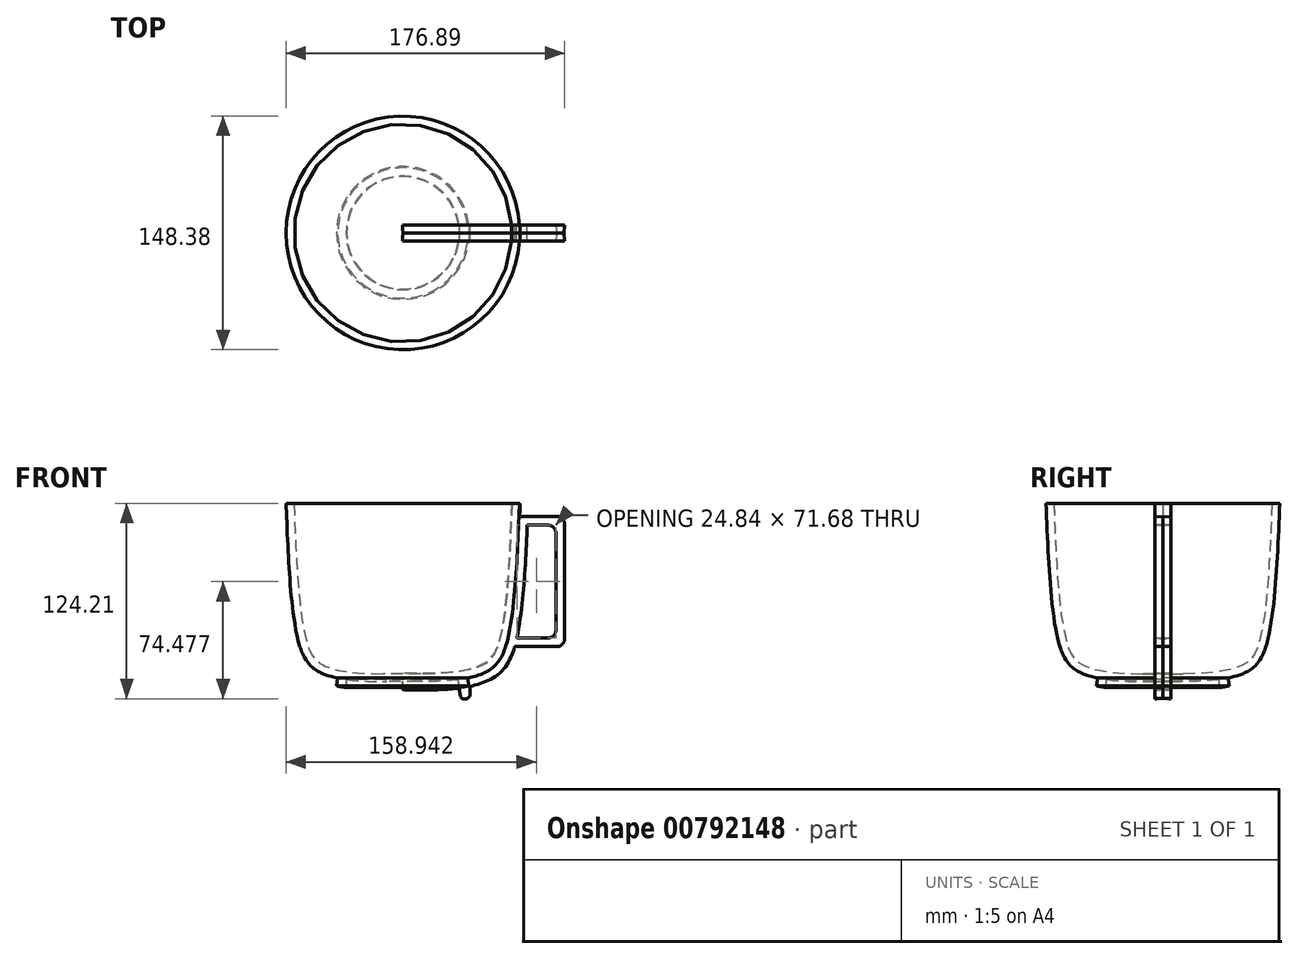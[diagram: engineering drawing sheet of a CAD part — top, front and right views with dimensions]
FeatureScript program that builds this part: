
annotation { "Feature Type Name" : "Feature", "Feature Type Description" : "" }
export const myFeature = defineFeature(function(context is Context, id is Id, definition is map)
    precondition{}
    {
        {
            var Q0;
            Q0=qCreatedBy(makeId("Front.planeOp"),FACE);
            var sketch = newSketch(context, id + "F0", { "sketchPlane" : qUnion([Q0])});
            skFitSpline(sketch, "E0", {"points": [v(74.37, 56.66) * mm, v(67.02, -32.92) * mm, v(51.64, -55.65) * mm, v(-23.23, -60) * mm], "startDerivative": vector(-9.7, -255.08) * mm, "endDerivative": vector(-242.27, 10.34) * mm});
            skFitSpline(sketch, "E1", {"points": [v(41.42, -58.78) * mm, v(41.61, -71.03) * mm, v(38.6, -71.7) * mm, v(37.27, -71.36) * mm, v(35.72, -59.72) * mm], "startDerivative": vector(7.18, -45.02) * mm, "endDerivative": vector(-2.54, 45.05) * mm});
            skFitSpline(sketch, "E2.0", {"points": [v(69.38, 56.85) * mm, v(69.17, 51.53) * mm, v(68.77, 40.91) * mm, v(68.1, 25.32) * mm, v(67.26, 10.36) * mm, v(66.22, -3.63) * mm, v(65.1, -14.23) * mm, v(64.03, -21.9) * mm, v(63.28, -26.32) * mm, v(62.63, -29.6) * mm, v(62.12, -31.94) * mm, v(61.6, -34.13) * mm, v(60.84, -36.84) * mm, v(59.83, -39.87) * mm, v(58.44, -42.92) * mm, v(56.86, -45.44) * mm, v(55.04, -47.54) * mm, v(53.22, -49.04) * mm, v(51.5, -50.13) * mm, v(50.05, -50.9) * mm, v(48.42, -51.62) * mm, v(46, -52.51) * mm, v(42.51, -53.5) * mm, v(37.7, -54.43) * mm, v(30.53, -55.37) * mm, v(20.35, -56) * mm, v(6.7, -56.06) * mm, v(-7.9, -55.65) * mm, v(-17.97, -55.22) * mm, v(-23.02, -55) * mm]});
            skLineSegment(sketch, "E3", {"start": v(69.2, 51.98) * mm, "end": v(74.2, 51.98) * mm});
            skLineSegment(sketch, "E4", {"start": v(0, 0) * mm, "end": v(0, -74.7) * mm});
            skLineSegment(sketch, "E5.bottom", {"start": v(97.44, 38.6) * mm, "end": v(78.67, 38.6) * mm});
            skLineSegment(sketch, "E5.top", {"start": v(97.44, -33.6) * mm, "end": v(72, -33.6) * mm});
            skLineSegment(sketch, "E5.left", {"start": v(97.44, 38.6) * mm, "end": v(97.44, -33.6) * mm});
            skLineSegment(sketch, "E6.0", {"start": v(102.44, 43.6) * mm, "end": v(73.87, 43.6) * mm});
            skLineSegment(sketch, "E6.1", {"start": v(102.44, 43.6) * mm, "end": v(102.44, -38.6) * mm});
            skLineSegment(sketch, "E6.2", {"start": v(102.44, -38.6) * mm, "end": v(65.5, -38.6) * mm});
            skFitSpline(sketch, "E7.0", {"points": [v(69.38, 56.85) * mm, v(69.17, 51.53) * mm, v(68.77, 40.91) * mm, v(68.1, 25.32) * mm, v(67.26, 10.36) * mm, v(66.22, -3.63) * mm, v(65.1, -14.23) * mm, v(64.03, -21.9) * mm, v(63.28, -26.32) * mm, v(62.63, -29.6) * mm, v(62.12, -31.94) * mm, v(61.6, -34.13) * mm, v(60.84, -36.84) * mm, v(59.83, -39.87) * mm, v(58.44, -42.92) * mm, v(56.86, -45.44) * mm, v(55.04, -47.54) * mm, v(53.22, -49.04) * mm, v(51.5, -50.13) * mm, v(50.05, -50.9) * mm, v(48.42, -51.62) * mm, v(46, -52.51) * mm, v(42.51, -53.5) * mm, v(37.7, -54.43) * mm, v(30.53, -55.37) * mm, v(20.35, -56) * mm, v(6.7, -56.06) * mm, v(-7.9, -55.65) * mm, v(-17.97, -55.22) * mm, v(-23.02, -55) * mm]});
            skFitSpline(sketch, "E8.trimOffspring", {"points": [v(79.37, 56.47) * mm, v(79.17, 51.15) * mm, v(78.76, 40.52) * mm, v(78.08, 24.83) * mm, v(77.24, 9.73) * mm, v(76.36, -2.13) * mm, v(75.5, -11.04) * mm, v(74.75, -17.4) * mm, v(73.92, -23.41) * mm, v(73.12, -28.1) * mm, v(72.43, -31.63) * mm, v(71.87, -34.18) * mm, v(71.28, -36.62) * mm, v(70.41, -39.76) * mm, v(69.17, -43.46) * mm, v(67.32, -47.58) * mm, v(64.98, -51.36) * mm, v(62.06, -54.73) * mm, v(58.54, -57.62) * mm, v(55.14, -59.59) * mm, v(52.15, -60.9) * mm, v(49, -62.07) * mm, v(44.77, -63.25) * mm, v(39.26, -64.31) * mm, v(31.38, -65.34) * mm, v(20.61, -66) * mm, v(6.55, -66.06) * mm, v(-8.28, -65.64) * mm, v(-18.4, -65.2) * mm, v(-23.44, -65) * mm]});
            skSolve(sketch);
        }
        {
            var Q0;
            {var subQ0=sQuery(id+"F0.wireOp",EDGE,"E3");var subQ1=sQuery(id+"F0.wireOp",EDGE,"E0");var subQ2=makeQuery(id+"F0.imprint","INTERSECT",VERTEX,{"derivedFrom":[subQ1,subQ0]});Q0=makeQuery(id+"F0.imprint","IMPRINT",FACE,{"disambiguationData":[TD([[makeQuery(id+"F0.imprint","IMPRINT",EDGE,{"disambiguationData":[TD([[subQ2,-1.0]])],"derivedFrom":subQ1}),-1.0]])]});}
            var Q1;
            {var subQ0=sQuery(id+"F0.wireOp",EDGE,"E6.0");var subQ1=sQuery(id+"F0.wireOp",EDGE,"E0");var subQ2=makeQuery(id+"F0.imprint","INTERSECT",VERTEX,{"derivedFrom":[subQ1,subQ0]});Q1=makeQuery(id+"F0.imprint","IMPRINT",FACE,{"disambiguationData":[TD([[makeQuery(id+"F0.imprint","IMPRINT",EDGE,{"disambiguationData":[TD([[subQ2,-1.0]])],"derivedFrom":subQ1}),-1.0]])]});}
            var Q2;
            {var subQ0=sQuery(id+"F0.wireOp",EDGE,"E5.bottom");var subQ1=sQuery(id+"F0.wireOp",EDGE,"E0");var subQ2=makeQuery(id+"F0.imprint","INTERSECT",VERTEX,{"derivedFrom":[subQ1,subQ0]});Q2=makeQuery(id+"F0.imprint","IMPRINT",FACE,{"disambiguationData":[TD([[makeQuery(id+"F0.imprint","IMPRINT",EDGE,{"disambiguationData":[TD([[subQ2,-1.0]])],"derivedFrom":subQ1}),-1.0]])]});}
            var Q3;
            {var subQ0=sQuery(id+"F0.wireOp",EDGE,"E1");var subQ1=sQuery(id+"F0.wireOp",EDGE,"E0");var subQ5=makeQuery(id+"F0.imprint","INTERSECT",VERTEX,{"disambiguationData":[OD(0.0)],"derivedFrom":[subQ1,subQ0]});Q3=makeQuery(id+"F0.imprint","IMPRINT",FACE,{"disambiguationData":[TD([[makeQuery(id+"F0.imprint","IMPRINT",EDGE,{"disambiguationData":[TD([[subQ5,1.0]])],"derivedFrom":subQ1}),-1.0]])]});}
            var Q4;
            {var subQ0=sQuery(id+"F0.wireOp",EDGE,"E6.2");var subQ1=sQuery(id+"F0.wireOp",EDGE,"E0");var subQ2=makeQuery(id+"F0.imprint","INTERSECT",VERTEX,{"derivedFrom":[subQ1,subQ0]});Q4=makeQuery(id+"F0.imprint","IMPRINT",FACE,{"disambiguationData":[TD([[makeQuery(id+"F0.imprint","IMPRINT",EDGE,{"disambiguationData":[TD([[subQ2,1.0]])],"derivedFrom":subQ1}),-1.0]])]});}
            var Q5;
            {var subQ0=sQuery(id+"F0.wireOp",EDGE,"E1");Q5=makeQuery(id+"F0.imprint","IMPRINT",FACE,{"disambiguationData":[TD([[makeQuery(id+"F0.imprint","IMPRINT",EDGE,{"derivedFrom":subQ0}),-1.0]])]});}
            var Q6;
            Q6=sQuery(id+"F0.wireOp",EDGE,"E4");
            revolve(context, id + "F1", {"surfaceOperationType" : NewSurfaceOperationType.NEW, "entities" : qUnion([Q0, Q1, Q2, Q3, Q4, Q5]), "axis" : qUnion([Q6]), "revolveType" : RevolveType.FULL});
        }
        {
            var Q0;
            Q0 = qSketchRegion(id + "F0", true);
            extrude(context, id + "F2", {"entities" : qUnion([Q0]), "operationType" : NewBodyOperationType.ADD, "endBound" : BoundingType.SYMMETRIC, "depth" : 10 * mm, "offsetDistance" : 25 * mm, "hasDraft" : true, "draftAngle" : 3 * degree});
        }
        {
            var Q0;
            {var subQ5=sQuery(id+"F0.wireOp",EDGE,"E8.trimOffspring");Q0=makeQuery(id+"F0.imprint","IMPRINT",FACE,{"disambiguationData":[TD([[makeQuery(id+"F0.imprint","IMPRINT",EDGE,{"derivedFrom":subQ5}),-1.0]])]});}
            extrude(context, id + "F3", {"entities" : qUnion([Q0]), "operationType" : NewBodyOperationType.ADD, "endBound" : BoundingType.SYMMETRIC, "depth" : 10 * mm, "offsetDistance" : 25 * mm});
        }
        {
            var Q0;
            Q0=makeQuery(id+"F2.*.split.splitOp","SPLIT",EDGE,{"derivedFrom":makeQuery(id+"F2.opExtrude","SWEPT_EDGE",EDGE,{"disambiguationData":[OSD([sQuery(id+"F0.wireOp",EDGE,"E6.0"),sQuery(id+"F0.wireOp",EDGE,"E6.1")])]}),"isFromBackBody":true});
            var Q1;
            Q1=makeQuery(id+"F2.*.split.splitOp","SPLIT",EDGE,{"derivedFrom":makeQuery(id+"F2.opExtrude","SWEPT_EDGE",EDGE,{"disambiguationData":[OSD([sQuery(id+"F0.wireOp",EDGE,"E6.0"),sQuery(id+"F0.wireOp",EDGE,"E6.1")])]})});
            var Q2;
            Q2=makeQuery(id+"F2.*.split.splitOp","SPLIT",EDGE,{"derivedFrom":makeQuery(id+"F2.opExtrude","SWEPT_EDGE",EDGE,{"disambiguationData":[OSD([sQuery(id+"F0.wireOp",EDGE,"E5.bottom"),sQuery(id+"F0.wireOp",EDGE,"E5.left")])]}),"isFromBackBody":true});
            var Q3;
            Q3=makeQuery(id+"F2.*.split.splitOp","SPLIT",EDGE,{"derivedFrom":makeQuery(id+"F2.opExtrude","SWEPT_EDGE",EDGE,{"disambiguationData":[OSD([sQuery(id+"F0.wireOp",EDGE,"E5.bottom"),sQuery(id+"F0.wireOp",EDGE,"E5.left")])]})});
            var Q4;
            Q4=makeQuery(id+"F2.*.split.splitOp","SPLIT",EDGE,{"derivedFrom":makeQuery(id+"F2.opExtrude","SWEPT_EDGE",EDGE,{"disambiguationData":[OSD([sQuery(id+"F0.wireOp",EDGE,"E5.top"),sQuery(id+"F0.wireOp",EDGE,"E5.left")])]}),"isFromBackBody":true});
            var Q5;
            Q5=makeQuery(id+"F2.*.split.splitOp","SPLIT",EDGE,{"derivedFrom":makeQuery(id+"F2.opExtrude","SWEPT_EDGE",EDGE,{"disambiguationData":[OSD([sQuery(id+"F0.wireOp",EDGE,"E5.top"),sQuery(id+"F0.wireOp",EDGE,"E5.left")])]})});
            var Q6;
            Q6=makeQuery(id+"F2.*.split.splitOp","SPLIT",EDGE,{"derivedFrom":makeQuery(id+"F2.opExtrude","SWEPT_EDGE",EDGE,{"disambiguationData":[OSD([sQuery(id+"F0.wireOp",EDGE,"E6.1"),sQuery(id+"F0.wireOp",EDGE,"E6.2")])]}),"isFromBackBody":true});
            var Q7;
            Q7=makeQuery(id+"F2.*.split.splitOp","SPLIT",EDGE,{"derivedFrom":makeQuery(id+"F2.opExtrude","SWEPT_EDGE",EDGE,{"disambiguationData":[OSD([sQuery(id+"F0.wireOp",EDGE,"E6.1"),sQuery(id+"F0.wireOp",EDGE,"E6.2")])]})});
            fillet(context, id + "F4", {"entities" : qUnion([Q0, Q1, Q2, Q3, Q4, Q5, Q6, Q7]), "radius" : 5 * mm, "tangentPropagation" : true, "allowEdgeOverflow" : false});
        }
    });
